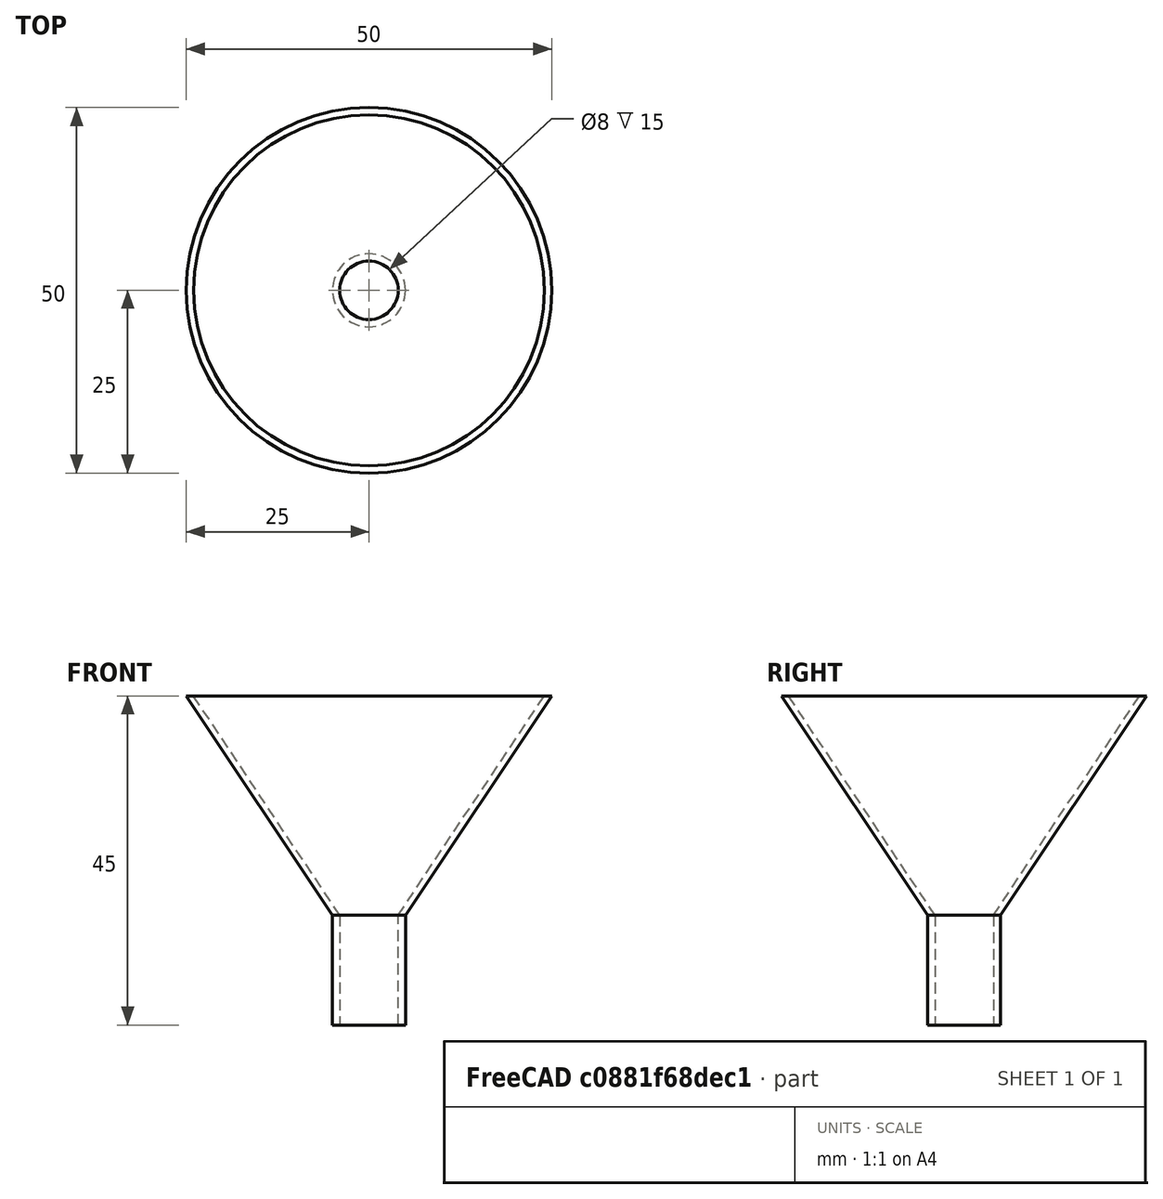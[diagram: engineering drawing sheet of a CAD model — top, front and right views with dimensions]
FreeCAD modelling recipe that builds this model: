
FCSTD DOCUMENT  (FreeCAD 0.21R33694 (Git))
Label: OJT1_T14R03_embut
License: All rights reserved
LicenseURL: http://en.wikipedia.org/wiki/All_rights_reserved
objects: Part::Cylinder×2, Part::Cone×2, Part::Cut×2
note: 6 computed .brp shape members not serialized (recipe doc carries the construction recipe); baked Part::Feature solids carry a one-line shape summary decoded from their .brp

FEATURE [Part::Cylinder] Cylinder
  Angle = 360
  AttacherType = Attacher::AttachEngine3D
  FirstAngle = 0
  Height = 15
  Radius = 5
  SecondAngle = 0
FEATURE [Part::Cone] Cone  label="cilindre_exterior"
  Angle = 360
  AttacherType = Attacher::AttachEngine3D
  Height = 30
  Radius1 = 5
  Radius2 = 25
FEATURE [Part::Cone] Cone001  label="cilindre_interior"
  Angle = 360
  AttacherType = Attacher::AttachEngine3D
  Height = 30
  Radius1 = 4
  Radius2 = 24
FEATURE [Part::Cut] Cut
  Base = -> Cone
  Placement = pos=(0,0,15) rot=(0,0,1;0rad)
  Refine = true
  Tool = -> Cone001
FEATURE [Part::Cylinder] Cylinder001
  Angle = 360
  AttacherType = Attacher::AttachEngine3D
  FirstAngle = 0
  Height = 15
  Radius = 4
  SecondAngle = 0
FEATURE [Part::Cut] Cut001
  Base = -> Cylinder
  Refine = true
  Tool = -> Cylinder001
